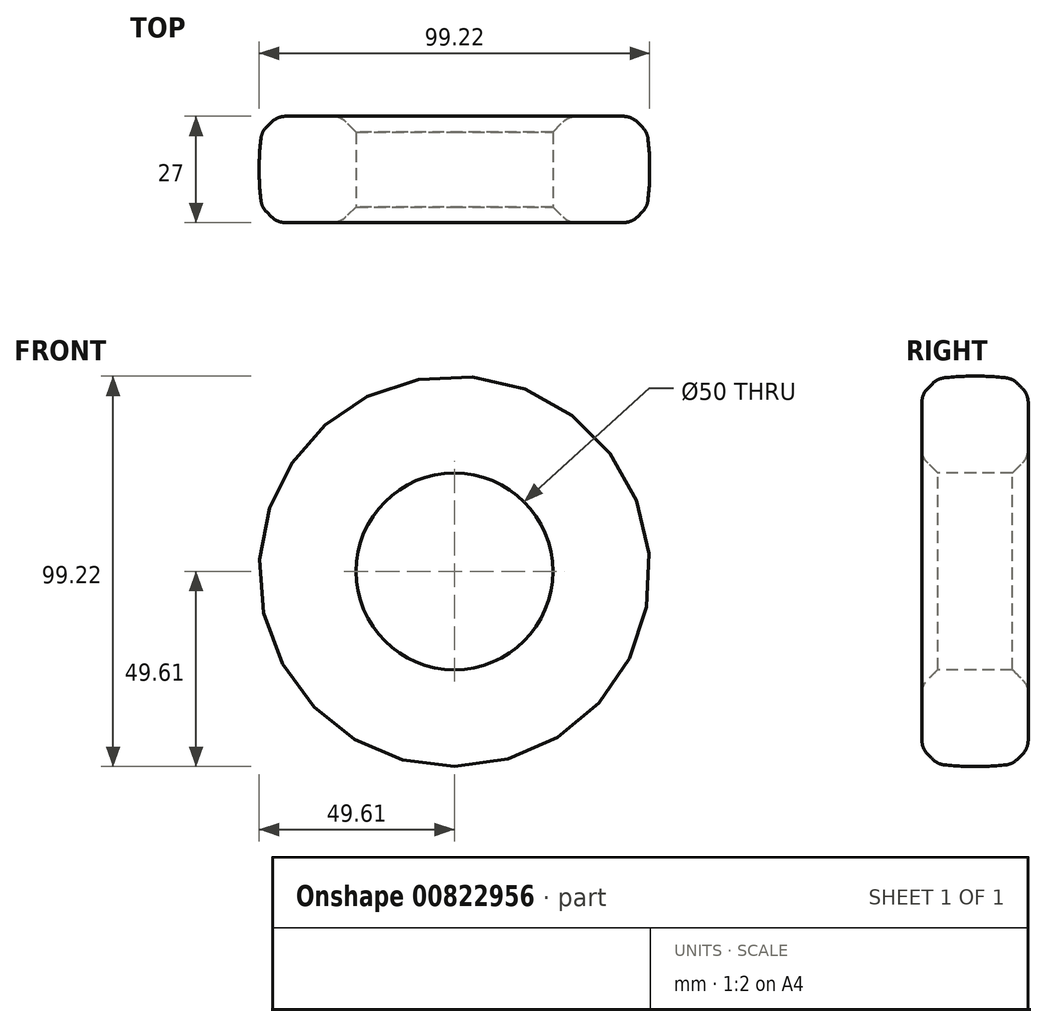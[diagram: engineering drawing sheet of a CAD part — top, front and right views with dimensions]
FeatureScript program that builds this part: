
annotation { "Feature Type Name" : "Feature", "Feature Type Description" : "" }
export const myFeature = defineFeature(function(context is Context, id is Id, definition is map)
    precondition{}
    {
        {
            var Q0;
            Q0=qCreatedBy(makeId("Top.planeOp"),FACE);
            var sketch = newSketch(context, id + "F0", { "sketchPlane" : qUnion([Q0])});
            skLineSegment(sketch, "E0", {"start": v(0, 0) * mm, "end": v(-63.9, 0) * mm, "construction": true});
            skLineSegment(sketch, "E1", {"start": v(0, 0) * mm, "end": v(0, 37.71) * mm, "construction": true});
            skLineSegment(sketch, "E2", {"start": v(-25, 9.5) * mm, "end": v(-29, 13.5) * mm});
            skLineSegment(sketch, "E3", {"start": v(-29, 13.5) * mm, "end": v(-45, 13.5) * mm});
            skLineSegment(sketch, "E4", {"start": v(-45, 13.5) * mm, "end": v(-49, 9.5) * mm});
            skLineSegment(sketch, "E5", {"start": v(-49, 9.5) * mm, "end": v(-50, 0) * mm});
            skLineSegment(sketch, "E6", {"start": v(-25, 9.5) * mm, "end": v(-25, 0) * mm});
            skLineSegment(sketch, "E7.MirrorCS", {"start": v(-29, -13.5) * mm, "end": v(-45, -13.5) * mm});
            skLineSegment(sketch, "E8.MirrorCS", {"start": v(-25, -9.5) * mm, "end": v(-29, -13.5) * mm});
            skLineSegment(sketch, "E9.MirrorCS", {"start": v(-25, -9.5) * mm, "end": v(-25, 0) * mm});
            skLineSegment(sketch, "E10.MirrorCS", {"start": v(-45, -13.5) * mm, "end": v(-49, -9.5) * mm});
            skLineSegment(sketch, "E11.MirrorCS", {"start": v(-49, -9.5) * mm, "end": v(-50, 0) * mm});
            skSolve(sketch);
        }
        {
            var Q0;
            Q0 = qSketchRegion(id + "F0", true);
            var Q1;
            Q1=makeQuery(id+"F0.imprint","IMPRINT",FACE,{"disambiguationData":[TD([[makeQuery(id+"F0.imprint","IMPRINT",EDGE,{"derivedFrom":sQuery(id+"F0.wireOp",EDGE,"E2")}),1.0]])]});
            var Q2;
            Q2=sQuery(id+"F0.wireOp",EDGE,"E1");
            revolve(context, id + "F1", {"surfaceOperationType" : NewSurfaceOperationType.NEW, "entities" : qUnion([Q0, Q1]), "axis" : qUnion([Q2]), "revolveType" : RevolveType.FULL});
        }
        {
            var Q0;
            Q0=makeQuery(id+"F1.opRevolve","SWEPT_EDGE",EDGE,{"disambiguationData":[OSD([sQuery(id+"F0.wireOp",EDGE,"E7.MirrorCS"),sQuery(id+"F0.wireOp",EDGE,"E8.MirrorCS")])]});
            var Q1;
            Q1=makeQuery(id+"F1.opRevolve","SWEPT_EDGE",EDGE,{"disambiguationData":[OSD([sQuery(id+"F0.wireOp",EDGE,"E7.MirrorCS"),sQuery(id+"F0.wireOp",EDGE,"E10.MirrorCS")])]});
            var Q2;
            Q2=makeQuery(id+"F1.opRevolve","SWEPT_EDGE",EDGE,{"disambiguationData":[OSD([sQuery(id+"F0.wireOp",EDGE,"E10.MirrorCS"),sQuery(id+"F0.wireOp",EDGE,"E11.MirrorCS")])]});
            var Q3;
            Q3=makeQuery(id+"F1.opRevolve","SWEPT_EDGE",EDGE,{"disambiguationData":[OSD([sQuery(id+"F0.wireOp",EDGE,"E3"),sQuery(id+"F0.wireOp",EDGE,"E4")])]});
            var Q4;
            Q4=makeQuery(id+"F1.opRevolve","SWEPT_EDGE",EDGE,{"disambiguationData":[OSD([sQuery(id+"F0.wireOp",EDGE,"E2"),sQuery(id+"F0.wireOp",EDGE,"E3")])]});
            var Q5;
            Q5=makeQuery(id+"F1.opRevolve","SWEPT_EDGE",EDGE,{"disambiguationData":[OSD([sQuery(id+"F0.wireOp",EDGE,"E4"),sQuery(id+"F0.wireOp",EDGE,"E5")])]});
            fillet(context, id + "F2", {"entities" : qUnion([Q0, Q1, Q2, Q3, Q4, Q5]), "radius" : 5 * mm, "tangentPropagation" : true, "allowEdgeOverflow" : false});
        }
        {
            var Q0;
            Q0=makeQuery(id+"F1.opRevolve","SWEPT_EDGE",EDGE,{"disambiguationData":[OSD([sQuery(id+"F0.wireOp",EDGE,"E5"),sQuery(id+"F0.wireOp",EDGE,"E11.MirrorCS")])]});
            fillet(context, id + "F3", {"entities" : qUnion([Q0]), "radius" : 70 * mm, "tangentPropagation" : true, "allowEdgeOverflow" : false});
        }
    });
